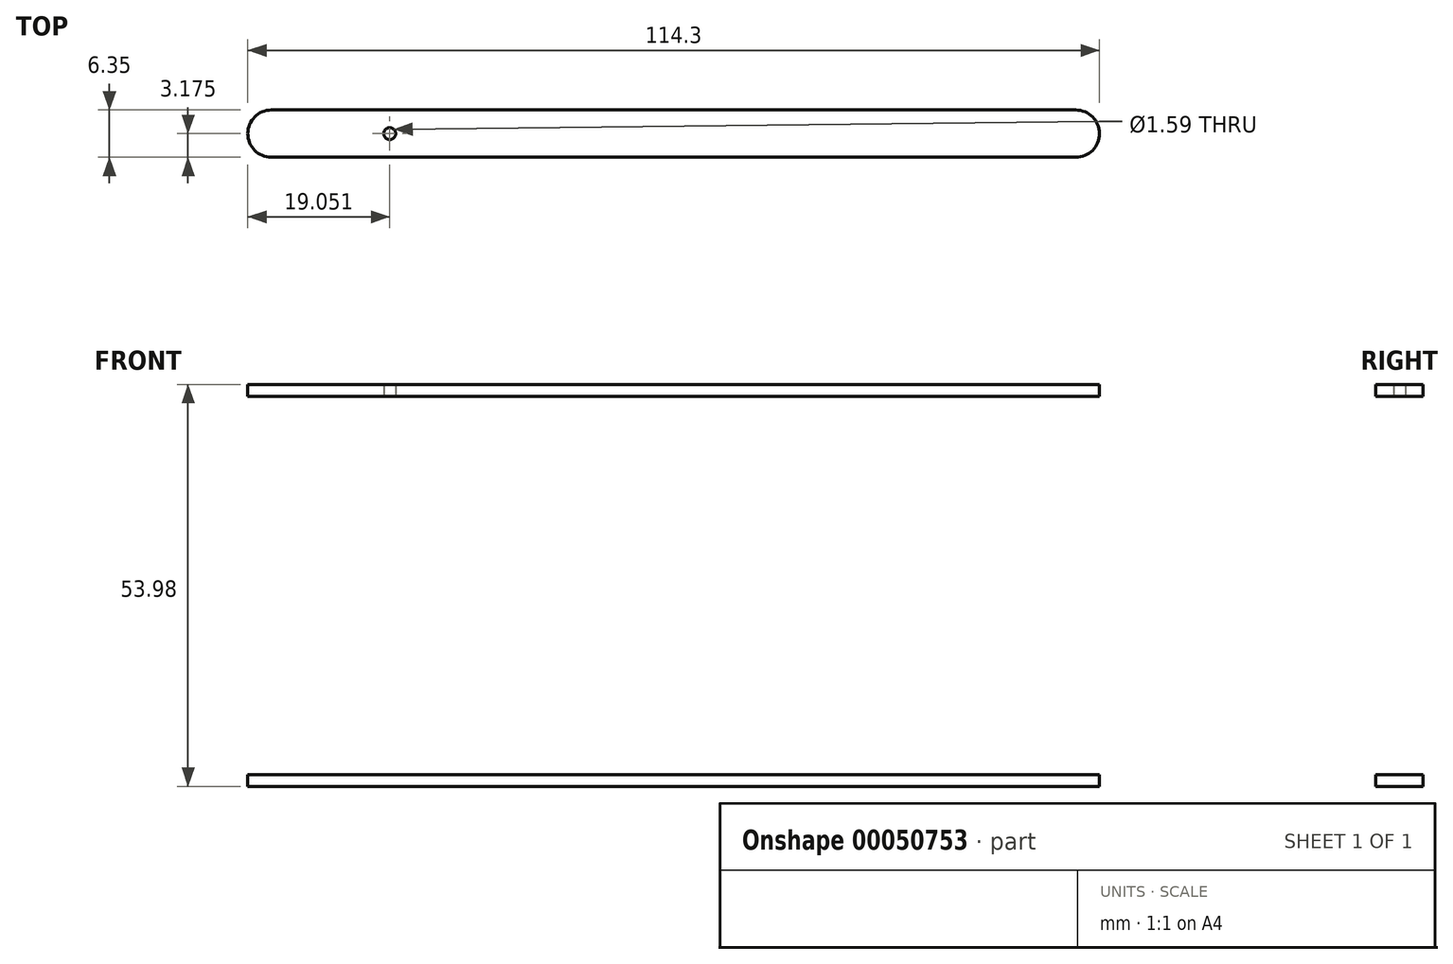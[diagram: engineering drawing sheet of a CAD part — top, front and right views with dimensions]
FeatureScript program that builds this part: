
annotation { "Feature Type Name" : "Feature", "Feature Type Description" : "" }
export const myFeature = defineFeature(function(context is Context, id is Id, definition is map)
    precondition{}
    {
        {
            var Q0;
            Q0=qCreatedBy(makeId("Top.planeOp"),FACE);
            var sketch = newSketch(context, id + "F0", { "sketchPlane" : qUnion([Q0])});
            skLineSegment(sketch, "E0", {"start": v(-8.34, 16.37) * mm, "end": v(99.6, 16.37) * mm});
            skLineSegment(sketch, "E1", {"start": v(-11.52, 19.54) * mm, "end": v(-11.52, 19.54) * mm});
            skLineSegment(sketch, "E2", {"start": v(-8.34, 22.72) * mm, "end": v(99.6, 22.72) * mm});
            skLineSegment(sketch, "E3", {"start": v(102.78, 19.54) * mm, "end": v(102.78, 19.54) * mm});
            skPoint(sketch, "E4.visualSharp", {"position": v(-11.52, 22.72) * mm});
            skArc(sketch, "E4.filletArc", {"start": v(-8.34, 22.72) * mm, "mid": v(-10.59, 21.79) * mm, "end": v(-11.52, 19.54) * mm});
            skPoint(sketch, "E5.visualSharp", {"position": v(-11.52, 16.37) * mm});
            skArc(sketch, "E5.filletArc", {"start": v(-11.52, 19.54) * mm, "mid": v(-10.59, 17.3) * mm, "end": v(-8.34, 16.37) * mm});
            skPoint(sketch, "E6.visualSharp", {"position": v(102.78, 22.72) * mm});
            skArc(sketch, "E6.filletArc", {"start": v(102.78, 19.54) * mm, "mid": v(101.85, 21.79) * mm, "end": v(99.6, 22.72) * mm});
            skPoint(sketch, "E7.visualSharp", {"position": v(102.78, 16.37) * mm});
            skArc(sketch, "E7.filletArc", {"start": v(99.6, 16.37) * mm, "mid": v(101.85, 17.3) * mm, "end": v(102.78, 19.54) * mm});
            skSolve(sketch);
        }
        {
            var Q0;
            Q0=makeQuery(id+"F0.imprint","IMPRINT",FACE,{"disambiguationData":[TD([[makeQuery(id+"F0.imprint","IMPRINT",EDGE,{"derivedFrom":sQuery(id+"F0.wireOp",EDGE,"E0")}),1.0]])]});
            extrude(context, id + "F1", {"entities" : qUnion([Q0]), "depth" : 1.59 * mm});
        }
        {
            var Q0;
            Q0=makeQuery(id+"F1.opExtrude","CAP_FACE",FACE,{"disambiguationData":[OSD([sQuery(id+"F0.wireOp",EDGE,"E0"),sQuery(id+"F0.wireOp",EDGE,"E2"),sQuery(id+"F0.wireOp",EDGE,"E4.filletArc"),sQuery(id+"F0.wireOp",EDGE,"E5.filletArc"),sQuery(id+"F0.wireOp",EDGE,"E6.filletArc"),sQuery(id+"F0.wireOp",EDGE,"E7.filletArc")])],"isStart":false});
            cPlane(context, id + "F2", {"entities" : qUnion([Q0]), "cplaneType" : CPlaneType.OFFSET, "offset" : 50.8 * mm, "width" : 152.4 * mm, "height" : 152.4 * mm});
        }
        {
            var Q0;
            Q0=qCreatedBy(id+"F2.planeOp",FACE);
            var sketch = newSketch(context, id + "F3", { "sketchPlane" : qUnion([Q0])});
            skArc(sketch, "E8.0.0", {"start": v(-8.34, 22.72) * mm, "mid": v(-11.52, 19.54) * mm, "end": v(-8.34, 16.37) * mm});
            skLineSegment(sketch, "E8.0.1", {"start": v(-8.34, 16.37) * mm, "end": v(99.6, 16.37) * mm});
            skArc(sketch, "E8.0.2", {"start": v(99.6, 16.37) * mm, "mid": v(102.78, 19.54) * mm, "end": v(99.6, 22.72) * mm});
            skLineSegment(sketch, "E8.0.3", {"start": v(99.6, 22.72) * mm, "end": v(-8.34, 22.72) * mm});
            skCircle(sketch, "E9", {"center": v(7.53, 19.54) * mm, "radius": 0.8 * mm});
            skLineSegment(sketch, "E10", {"start": v(7.53, 22.72) * mm, "end": v(7.53, 16.37) * mm});
            skSolve(sketch);
        }
        {
            var Q0;
            Q0 = qSketchRegion(id + "F3", true);
            extrude(context, id + "F4", {"entities" : qUnion([Q0]), "depth" : 1.59 * mm});
        }
    });
